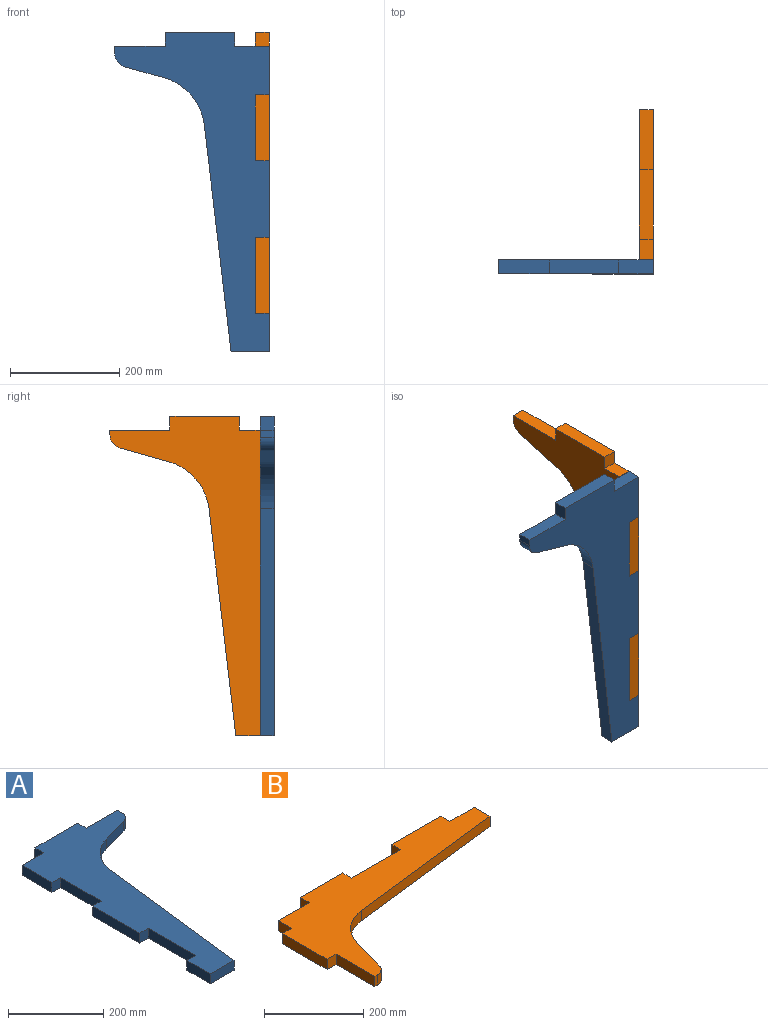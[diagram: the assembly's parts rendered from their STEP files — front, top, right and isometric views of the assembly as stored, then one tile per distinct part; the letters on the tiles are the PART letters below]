
ASSEMBLY  parts=2 mates=1
PART A: 22 faces, bbox 283x584.2x25.4 mm
  f0: plane 25.4x25.4mm, normal (0,-1,0), area 645.2mm2, adj f1,f19,f20,f21
  f1: plane 139.7x25.4mm, normal (-1,0,0), area 3548.4mm2, adj f0,f2,f20,f21
  f2: plane 25.4x25.4mm, normal (0,1,0), area 645.2mm2, adj f1,f3,f20,f21
  f3: plane 69.85x25.4mm, normal (-1,0,0), area 1774.2mm2, adj f2,f4,f20,f21
  f4: plane 70.05x25.4mm, normal (0,-1,0), area 1779.1mm2, adj f3,f5,f20,f21
  f5: plane 415.09x48.99mm, normal (0.99,-0.12,0), area 10616.3mm2, adj f4,f6,f20,f21
  f6: cylinder r=101.6mm len=85.9mm, axis (0,0,-1), area 3043.6mm2, adj f5,f7,f20,f21
  f7: plane 71.98x25.4mm, normal (0.27,-0.96,0), area 1899mm2, adj f6,f8,f20,f21
  f8: cylinder r=25.4mm len=25.4mm, axis (0,0,-1), area 836.7mm2, adj f7,f9,f20,f21
  f9: plane 25.4x13.13mm, normal (1,0,0), area 333.6mm2, adj f8,f10,f20,f21
  f10: plane 92.46x25.4mm, normal (0,1,0), area 2348.4mm2, adj f9,f11,f20,f21
  f11: plane 25.4x25.4mm, normal (1,0,0), area 645.2mm2, adj f10,f12,f20,f21
  f12: plane 127x25.4mm, normal (0,1,0), area 3225.8mm2, adj f11,f13,f20,f21
  f13: plane 25.4x25.4mm, normal (-1,0,0), area 645.2mm2, adj f12,f14,f20,f21
  f14: plane 63.5x25.4mm, normal (0,1,0), area 1612.9mm2, adj f13,f15,f20,f21
  f15: plane 88.9x25.4mm, normal (-1,0,0), area 2258.1mm2, adj f14,f16,f20,f21
  f16: plane 25.4x25.4mm, normal (0,-1,0), area 645.2mm2, adj f15,f17,f20,f21
  f17: plane 120.65x25.4mm, normal (-1,0,0), area 3064.5mm2, adj f16,f18,f20,f21
  f18: plane 25.4x25.4mm, normal (0,1,0), area 645.2mm2, adj f17,f19,f20,f21
  f19: plane 139.7x25.4mm, normal (-1,0,0), area 3548.4mm2, adj f0,f18,f20,f21
  f20: plane 584.2x282.96mm, normal (0,0,1), area 63053.5mm2, adj f0,f1,f2,f3,f4,f5,f6,f7
  f21: plane 584.2x282.96mm, normal (0,0,-1), area 63053.5mm2, adj f0,f1,f2,f3,f4,f5,f6,f7
PART B: 22 faces, bbox 584.2x300.4x25.4 mm
  f0: plane 109.86x25.4mm, normal (-1,0,0), area 2790.5mm2, adj f1,f19,f20,f21
  f1: plane 25.4x8.24mm, normal (0,-1,0), area 209.4mm2, adj f0,f2,f20,f21
  f2: cylinder r=25.4mm len=25.4mm, axis (0,0,-1), area 836.7mm2, adj f1,f3,f20,f21
  f3: plane 89.39x25.4mm, normal (0.96,-0.27,0), area 2358.3mm2, adj f2,f4,f20,f21
  f4: cylinder r=101.6mm len=85.9mm, axis (0,0,-1), area 3043.6mm2, adj f3,f5,f20,f21
  f5: plane 415.09x48.99mm, normal (0.12,-0.99,0), area 10616.3mm2, adj f4,f6,f20,f21
  f6: plane 44.65x25.4mm, normal (1,0,0), area 1134mm2, adj f5,f7,f20,f21
  f7: plane 69.85x25.4mm, normal (0,1,0), area 1774.2mm2, adj f6,f8,f20,f21
  f8: plane 25.4x25.4mm, normal (1,0,0), area 645.2mm2, adj f7,f9,f20,f21
  f9: plane 139.7x25.4mm, normal (0,1,0), area 3548.4mm2, adj f8,f10,f20,f21
  f10: plane 25.4x25.4mm, normal (-1,0,0), area 645.2mm2, adj f9,f11,f20,f21
  f11: plane 139.7x25.4mm, normal (0,1,0), area 3548.4mm2, adj f10,f12,f20,f21
  f12: plane 25.4x25.4mm, normal (1,0,0), area 645.2mm2, adj f11,f13,f20,f21
  f13: plane 120.65x25.4mm, normal (0,1,0), area 3064.5mm2, adj f12,f14,f20,f21
  f14: plane 25.4x25.4mm, normal (-1,0,0), area 645.2mm2, adj f13,f15,f20,f21
  f15: plane 88.9x25.4mm, normal (0,1,0), area 2258.1mm2, adj f14,f16,f20,f21
  f16: plane 38.1x25.4mm, normal (-1,0,0), area 967.7mm2, adj f15,f17,f20,f21
  f17: plane 25.4x25.4mm, normal (0,1,0), area 645.2mm2, adj f16,f18,f20,f21
  f18: plane 127x25.4mm, normal (-1,0,0), area 3225.8mm2, adj f17,f19,f20,f21
  f19: plane 25.4x25.4mm, normal (0,-1,0), area 645.2mm2, adj f0,f18,f20,f21
  f20: plane 584.2x300.36mm, normal (0,0,1), area 62606.8mm2, adj f0,f1,f2,f3,f4,f5,f6,f7
  f21: plane 584.2x300.36mm, normal (0,0,-1), area 62606.8mm2, adj f0,f1,f2,f3,f4,f5,f6,f7
PLACE A rot(axis=(0,0.71,0.71),180deg) t=(-413,-288.88,-589.73)mm
PLACE B rot(axis=(-0.71,0,0.71),180deg) t=(806.2,318.7,-849.48)mm
MATE fastened A.f16 <-> B.f14  axis (0,0,1) through (793.5,-276.18,-94.43)mm
